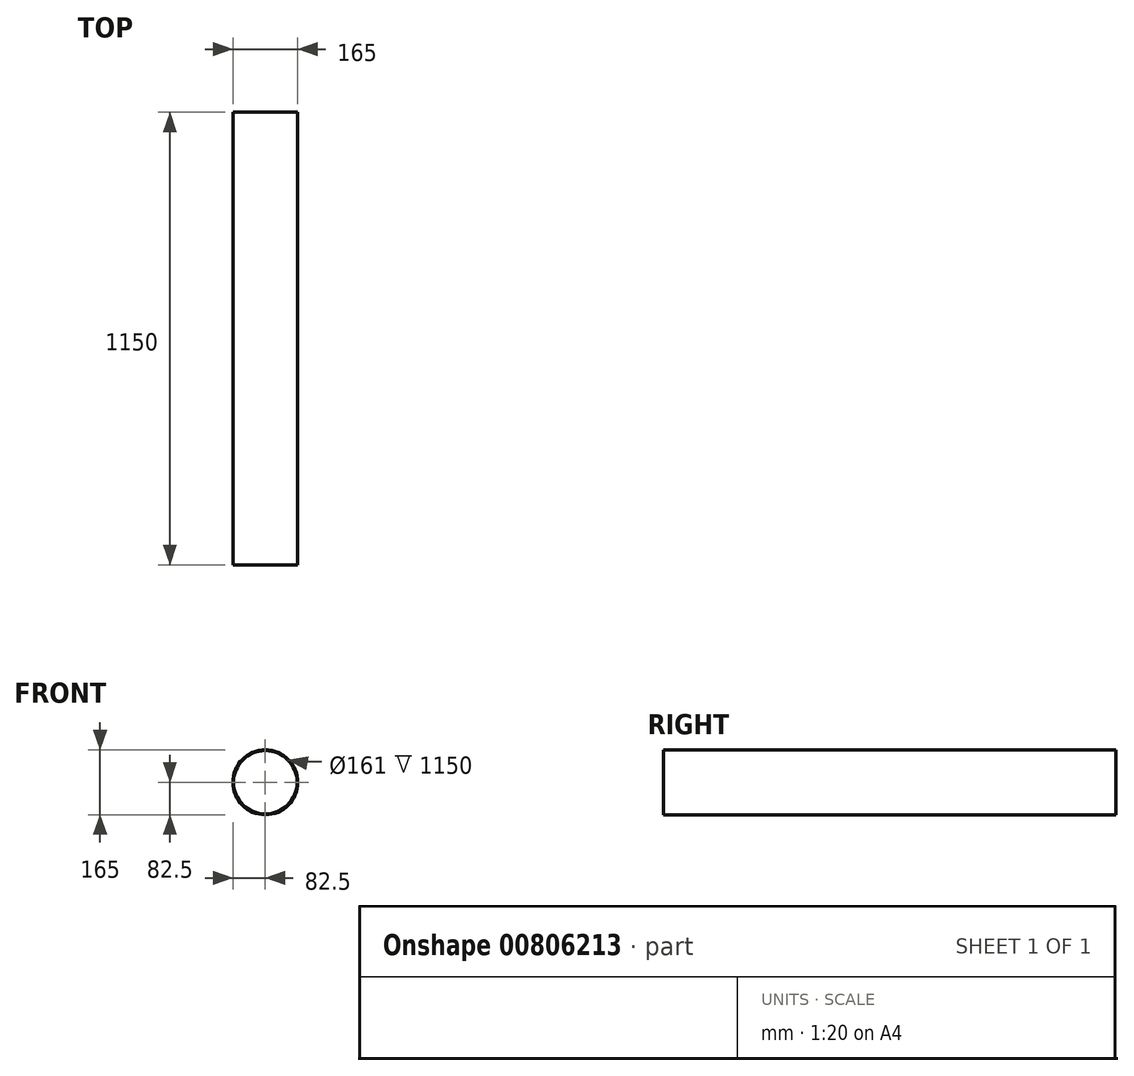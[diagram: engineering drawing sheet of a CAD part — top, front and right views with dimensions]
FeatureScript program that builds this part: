
annotation { "Feature Type Name" : "Feature", "Feature Type Description" : "" }
export const myFeature = defineFeature(function(context is Context, id is Id, definition is map)
    precondition{}
    {
        {
            var Q0;
            Q0=qCreatedBy(makeId("Front.planeOp"),FACE);
            var sketch = newSketch(context, id + "F0", { "sketchPlane" : qUnion([Q0])});
            skCircle(sketch, "E0", {"center": v(0, 0) * mm, "radius": 80.5 * mm});
            skCircle(sketch, "E1", {"center": v(0, 0) * mm, "radius": 82.5 * mm});
            skSolve(sketch);
        }
        {
            var Q0;
            Q0=qSketchRegion(id+"F0",true);
            extrude(context, id + "F1", {"entities" : qUnion([Q0]), "depth" : 1150 * mm, "offsetDistance" : 25 * mm});
        }
    });
